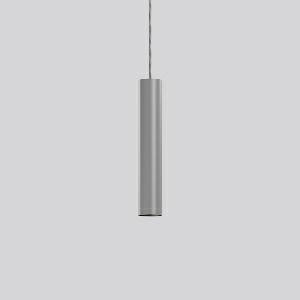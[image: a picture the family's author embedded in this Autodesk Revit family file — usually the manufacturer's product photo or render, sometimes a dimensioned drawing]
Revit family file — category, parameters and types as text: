
# Revit family: deecos_p_micro_911491_004_2_2bcb
name_source: partatom
category: Lighting Fixtures
units: mm (PartAtom-declared; Revit-internal decimal feet)

## family parameters
Cut with Voids When Loaded = No
Host = Face
Light Source = No
Part Type = Normal
Room Calculation Point = No
Round Connector Dimension = Use Diameter
Shared = No

## types (1)
- DEECOS P micro (1 x LED Modul 940, 1850 lm, 4000)
    Apparent Load = 16 VA
    CIE Flux Codes = 98 100 100 100 100
    Color Rendering = 92
    Color Temperature = 4000
    Default Elevation = 1800 mm
    Description = Series: DEECOS P micro
Cylindrical pendant luminaire. Housing: die-cast aluminium, powder-coated. Canopy made of powder-coated sheet steel with magnetic attachment. Optical assembly with reflector made of MIRO-Silver with 98% total light reflection for outstanding efficiency - can be changed without tools. Black plastic ring and recessed LED to prevent glare from the side. Best colour rendering index Ra>90. Transparent suspension cable 3 m, can be shortened. High quality converter without flickering and stroboscopic effect. 
Colour: silver
Diameter: 60 mm
Height: 340 mm
Suspension length: 3000 mm
Lamp: LED
Socket: without socket
Colour temperature: 4000K
Colour rendering index (CRI): 92
System power: 16 W
Rated luminous flux: 1850 lm
Luminous efficiency: 116 lm/W
Control gear: Regulated power supply
Protection class: I
Type of protection: IP 20
    Height = 340 mm
    Lamp = 1 x LED Modul 940
    Lamp Light Flux = 1850 lm
    Lamp count = 1
    Length = 60 mm  [stored 0.19685 ft]
    Lifetime = 50000 h
    Luminous efficacy = 116 lm/W
    Manufacturer = RZB
    ModVariant = No
    Model = 911491.004.2
    Mounting Place = Ceiling
    Mounting Type = Pendant
    Number of Poles = 1
    OnlyDefault = Yes
    Power Factor = 1
    Product Name = DEECOS P micro
    Product group = Pendant luminaires
    ProductGroupID = 902
    Protection Class = Protection class I
    Protection Degree = Degree of protection
    RLX_Detail_Level = 1
    RLX_Emergency_Light_Flux = 0 lm
    RLX_Emergency_Type = 0
    RLX_Emergency_Type_DB = No
    RlxData = <blob elided: 31233 chars, md5=b8857449>
    Socket = socket
    Standby Power = 0 W
    System Light Flux = 1850 lm
    System Power = 16 W
    Type Comments = Product without accessories
    Type Image = 911491.004.jpg
    URL = http://relux.com
    VarID = ---
    Voltage = 0 V
    Weight = 0.00 kg
    Width = 0 mm  [stored 0 ft]

note: [stored X ft] marks values corroborated as IEEE doubles in the binary element streams (Revit-internal decimal feet)

## geometry (parser evidence)
native form markers: Blend x4, Sweep x8
no freeform markers — native parametric forms only
